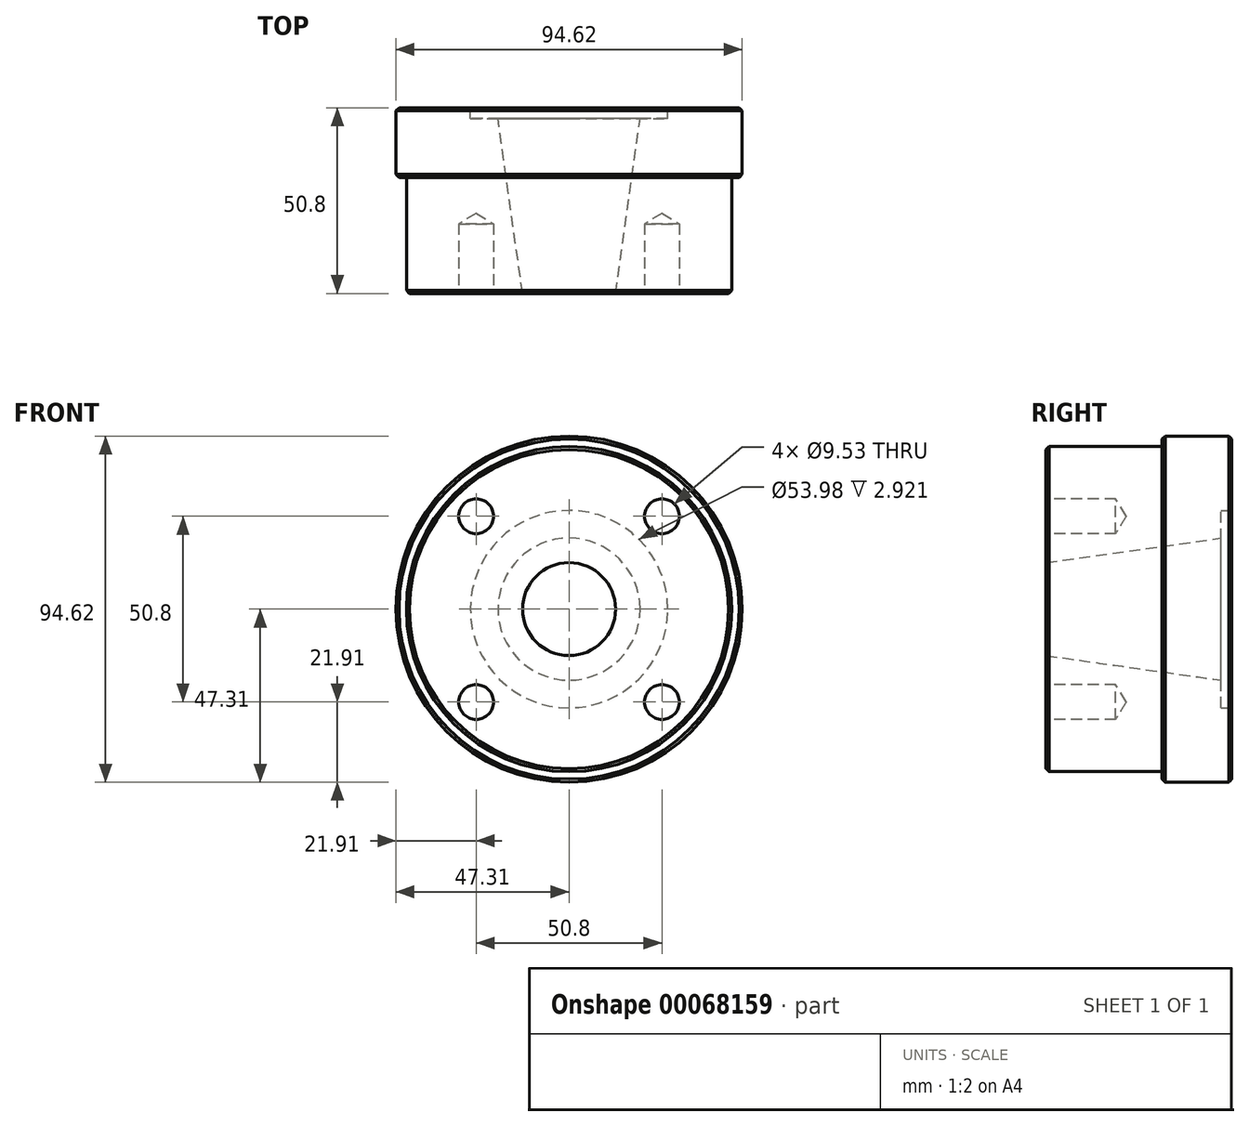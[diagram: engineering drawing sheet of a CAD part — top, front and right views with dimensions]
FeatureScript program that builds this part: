
annotation { "Feature Type Name" : "Feature", "Feature Type Description" : "" }
export const myFeature = defineFeature(function(context is Context, id is Id, definition is map)
    precondition{}
    {
        {
            var Q0;
            Q0=qCreatedBy(makeId("Front.planeOp"),FACE);
            var sketch = newSketch(context, id + "F0", { "sketchPlane" : qUnion([Q0])});
            skCircle(sketch, "E0", {"center": v(0, 0) * mm, "radius": 47.3 * mm});
            skCircle(sketch, "E1", {"center": v(0, 0) * mm, "radius": 44.45 * mm});
            skCircle(sketch, "E2", {"center": v(0, 0) * mm, "radius": 12.7 * mm});
            skSolve(sketch);
        }
        {
            var Q0;
            Q0=makeQuery(id+"F0.imprint","IMPRINT",FACE,{"disambiguationData":[TD([[makeQuery(id+"F0.imprint","IMPRINT",EDGE,{"derivedFrom":sQuery(id+"F0.wireOp",EDGE,"E0")}),1.0]])]});
            extrude(context, id + "F1", {"entities" : qUnion([Q0]), "depth" : 19.05 * mm});
        }
        {
            var Q0;
            Q0=makeQuery(id+"F0.imprint","IMPRINT",FACE,{"disambiguationData":[TD([[makeQuery(id+"F0.imprint","IMPRINT",EDGE,{"derivedFrom":sQuery(id+"F0.wireOp",EDGE,"E1")}),1.0]])]});
            extrude(context, id + "F2", {"entities" : qUnion([Q0]), "operationType" : NewBodyOperationType.ADD, "depth" : 50.8 * mm});
        }
        {
            var Q0;
            Q0=makeQuery(id+"F2.opExtrude","CAP_EDGE",EDGE,{"disambiguationData":[OSD([sQuery(id+"F0.wireOp",EDGE,"E2")])],"isStart":true});
            chamfer(context, id + "F3", {"entities" : qUnion([Q0]), "chamferType" : ChamferType.OFFSET_ANGLE, "width" : 50.8 * mm, "oppositeDirection" : true, "angle" : 8 * degree, "tangentPropagation" : true});
        }
        {
            var Q0;
            Q0=makeQuery(id+"F0.imprint","IMPRINT",FACE,{"disambiguationData":[TD([[makeQuery(id+"F0.imprint","IMPRINT",EDGE,{"derivedFrom":sQuery(id+"F0.wireOp",EDGE,"E1")}),1.0]])]});
            var sketch = newSketch(context, id + "F4", { "sketchPlane" : qUnion([Q0])});
            skCircle(sketch, "E3", {"center": v(0, 0) * mm, "radius": 26.99 * mm});
            skSolve(sketch);
        }
        {
            var Q0;
            Q0=makeQuery(id+"F4.imprint","IMPRINT",FACE,{"disambiguationData":[TD([[makeQuery(id+"F4.imprint","IMPRINT",EDGE,{"derivedFrom":sQuery(id+"F4.wireOp",EDGE,"E3")}),1.0]])]});
            extrude(context, id + "F5", {"entities" : qUnion([Q0]), "operationType" : NewBodyOperationType.REMOVE, "depth" : 2.92 * mm});
        }
        {
            var Q0;
            Q0=makeQuery(id+"F2.opExtrude","CAP_FACE",FACE,{"disambiguationData":[OSD([sQuery(id+"F0.wireOp",EDGE,"E1"),sQuery(id+"F0.wireOp",EDGE,"E2")])],"isStart":false});
            var sketch = newSketch(context, id + "F6", { "sketchPlane" : qUnion([Q0])});
            skPoint(sketch, "E4", {"position": v(-25.4, 25.4) * mm});
            skPoint(sketch, "E5.MirrorP", {"position": v(25.4, 25.4) * mm});
            skPoint(sketch, "E6.MirrorP", {"position": v(-25.4, -25.4) * mm});
            skPoint(sketch, "E7.MirrorP", {"position": v(25.4, -25.4) * mm});
            skSolve(sketch);
        }
        {
            var Q0;
            Q0=sQuery(id+"F6.wireOp",VERTEX,"E4");
            var Q1;
            Q1=sQuery(id+"F6.wireOp",VERTEX,"E5.MirrorP");
            var Q2;
            Q2=sQuery(id+"F6.wireOp",VERTEX,"E6.MirrorP");
            var Q3;
            Q3=sQuery(id+"F6.wireOp",VERTEX,"E7.MirrorP");
            var Q4;
            Q4=makeQuery(id+"F1.opExtrude","SWEPT_BODY",BODY,{"disambiguationData":[OSD([sQuery(id+"F0.wireOp",EDGE,"E0"),sQuery(id+"F0.wireOp",EDGE,"E1")])]});
            hole(context, id + "F7", {"style" : HoleStyle.SIMPLE, "holeDiameter" : 9.52 * mm, "endStyle" : HoleEndStyle.BLIND, "holeDepth" : 19.05 * mm, "locations" : qUnion([Q0, Q1, Q2, Q3]), "scope" : qUnion([Q4])});
        }
        {
            var Q0;
            Q0=makeQuery(id+"F2.opExtrude","CAP_EDGE",EDGE,{"disambiguationData":[OSD([sQuery(id+"F0.wireOp",EDGE,"E1")])],"isStart":false});
            var Q1;
            Q1=makeQuery(id+"F1.opExtrude","CAP_EDGE",EDGE,{"disambiguationData":[OSD([sQuery(id+"F0.wireOp",EDGE,"E0")])],"isStart":false});
            var Q2;
            Q2=makeQuery(id+"F1.opExtrude","CAP_EDGE",EDGE,{"disambiguationData":[OSD([sQuery(id+"F0.wireOp",EDGE,"E0")])],"isStart":true});
            chamfer(context, id + "F8", {"entities" : qUnion([Q0, Q1, Q2]), "width" : 0.81 * mm, "tangentPropagation" : true});
        }
    });
